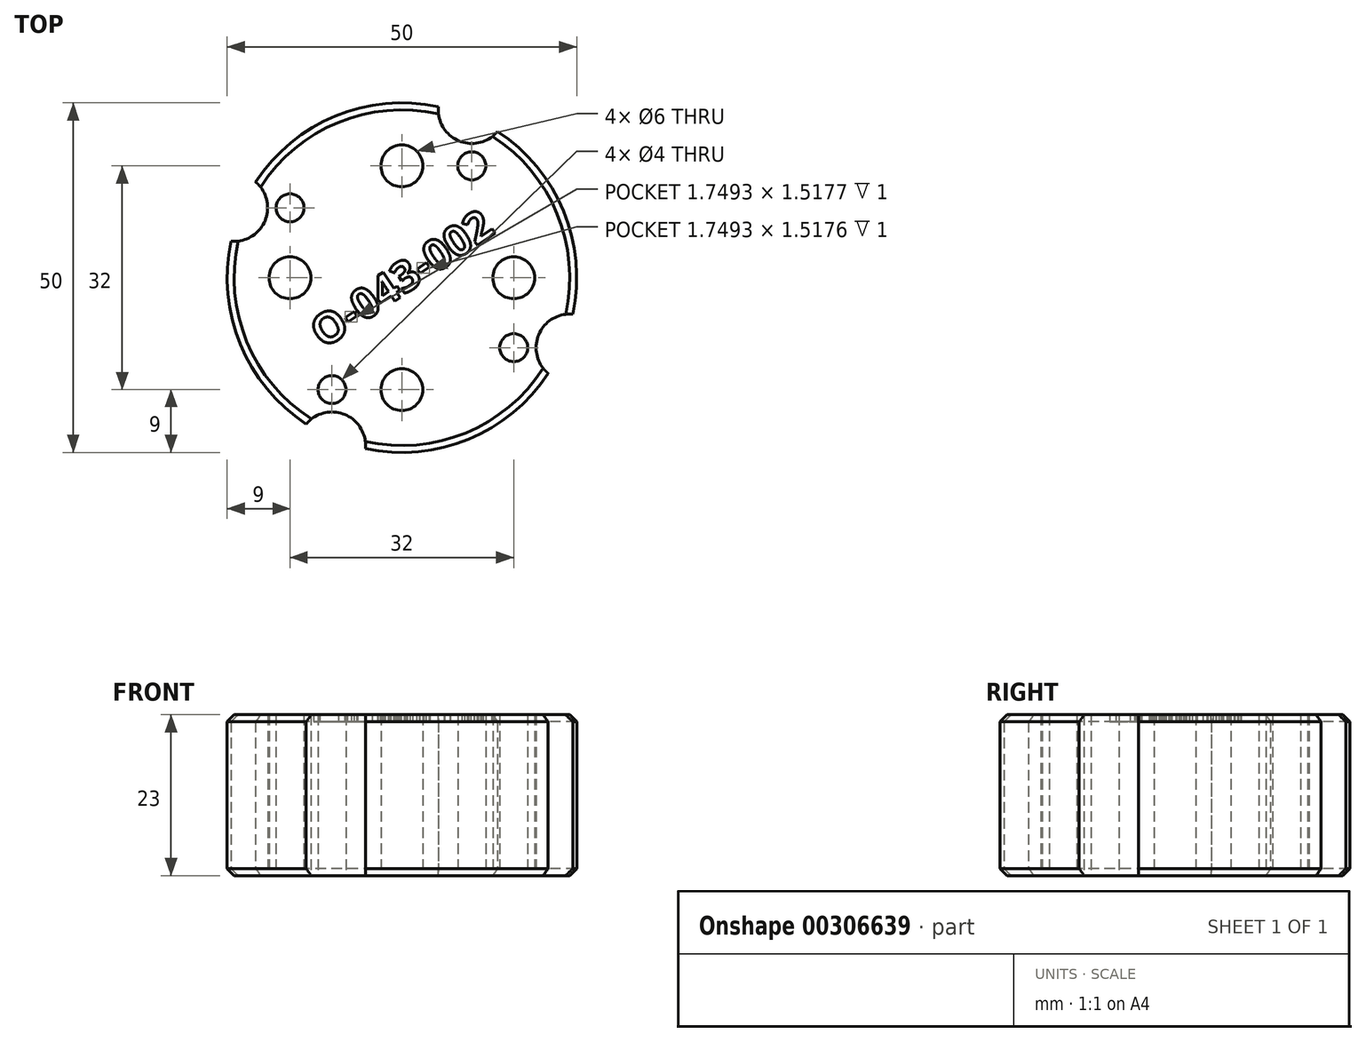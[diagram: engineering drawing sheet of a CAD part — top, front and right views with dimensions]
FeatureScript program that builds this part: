
annotation { "Feature Type Name" : "Feature", "Feature Type Description" : "" }
export const myFeature = defineFeature(function(context is Context, id is Id, definition is map)
    precondition{}
    {
        {
            var Q0;
            Q0=qCreatedBy(makeId("Top.planeOp"),FACE);
            var sketch = newSketch(context, id + "F0", { "sketchPlane" : qUnion([Q0])});
            skCircle(sketch, "E0", {"center": v(0, 16) * mm, "radius": 3 * mm});
            skPoint(sketch, "E1.center", {"position": v(0, 0) * mm});
            skCircle(sketch, "E2", {"center": v(10, 16) * mm, "radius": 2 * mm});
            skCircle(sketch, "E3.1.0", {"center": v(-16, 0) * mm, "radius": 3 * mm});
            skCircle(sketch, "E3.1.1", {"center": v(-16, 10) * mm, "radius": 2 * mm});
            skCircle(sketch, "E3.2.0", {"center": v(0, -16) * mm, "radius": 3 * mm});
            skCircle(sketch, "E3.2.1", {"center": v(-10, -16) * mm, "radius": 2 * mm});
            skCircle(sketch, "E3.3.0", {"center": v(16, 0) * mm, "radius": 3 * mm});
            skCircle(sketch, "E3.3.1", {"center": v(16, -10) * mm, "radius": 2 * mm});
            skCircle(sketch, "E4", {"center": v(0, 0) * mm, "radius": 25 * mm});
            skCircle(sketch, "E5", {"center": v(-24, 10) * mm, "radius": 4 * mm, "construction": true});
            skArc(sketch, "E6", {"start": v(-24.45, 5.22) * mm, "mid": v(-19.57, 8.15) * mm, "end": v(-20.92, 13.68) * mm});
            skCircle(sketch, "E7", {"center": v(-16, 10) * mm, "radius": 4.5 * mm, "construction": true});
            skArc(sketch, "E8.1.0", {"start": v(-5.22, -24.45) * mm, "mid": v(-8.15, -19.57) * mm, "end": v(-13.68, -20.92) * mm});
            skArc(sketch, "E8.2.0", {"start": v(24.45, -5.22) * mm, "mid": v(19.57, -8.15) * mm, "end": v(20.92, -13.68) * mm});
            skArc(sketch, "E8.3.0", {"start": v(5.22, 24.45) * mm, "mid": v(8.15, 19.57) * mm, "end": v(13.68, 20.92) * mm});
            skSolve(sketch);
        }
        {
            var Q0;
            Q0=makeQuery(id+"F0.imprint","IMPRINT",FACE,{"disambiguationData":[TD([[makeQuery(id+"F0.imprint","IMPRINT",EDGE,{"derivedFrom":sQuery(id+"F0.wireOp",EDGE,"E1.2.1")}),1.0]])]});
            var Q1;
            Q1=makeQuery(id+"F0.imprint","IMPRINT",FACE,{"disambiguationData":[TD([[makeQuery(id+"F0.imprint","IMPRINT",EDGE,{"derivedFrom":sQuery(id+"F0.wireOp",EDGE,"E1.3.1")}),1.0]])]});
            var Q2;
            Q2=makeQuery(id+"F0.imprint","IMPRINT",FACE,{"disambiguationData":[TD([[makeQuery(id+"F0.imprint","IMPRINT",EDGE,{"derivedFrom":sQuery(id+"F0.wireOp",EDGE,"E1.3.0")}),1.0]])]});
            var Q3;
            Q3=makeQuery(id+"F0.imprint","IMPRINT",FACE,{"disambiguationData":[TD([[makeQuery(id+"F0.imprint","IMPRINT",EDGE,{"derivedFrom":sQuery(id+"F0.wireOp",EDGE,"E1.2.0")}),1.0]])]});
            var Q4;
            Q4=makeQuery(id+"F0.imprint","IMPRINT",FACE,{"disambiguationData":[TD([[makeQuery(id+"F0.imprint","IMPRINT",EDGE,{"derivedFrom":sQuery(id+"F0.wireOp",EDGE,"5VkqoSrS-Cs9u-Mvgf-fKKW-AaG6FBBb1eUr")}),1.0]])]});
            var Q5;
            Q5=makeQuery(id+"F0.imprint","IMPRINT",FACE,{"disambiguationData":[TD([[makeQuery(id+"F0.imprint","IMPRINT",EDGE,{"derivedFrom":sQuery(id+"F0.wireOp",EDGE,"E1.1.0")}),1.0]])]});
            var Q6;
            Q6=makeQuery(id+"F0.imprint","IMPRINT",FACE,{"disambiguationData":[TD([[makeQuery(id+"F0.imprint","IMPRINT",EDGE,{"derivedFrom":sQuery(id+"F0.wireOp",EDGE,"E1.1.1")}),1.0]])]});
            var Q7;
            Q7=makeQuery(id+"F0.imprint","IMPRINT",FACE,{"disambiguationData":[TD([[makeQuery(id+"F0.imprint","IMPRINT",EDGE,{"derivedFrom":sQuery(id+"F0.wireOp",EDGE,"E0")}),-1.0]])]});
            extrude(context, id + "F1", {"entities" : qUnion([Q0, Q1, Q2, Q3, Q4, Q5, Q6, Q7]), "depth" : 23 * mm});
        }
        {
            var Q0;
            Q0=makeQuery(id+"F1.opExtrude","CAP_FACE",FACE,{"disambiguationData":[OSD([sQuery(id+"F0.wireOp",EDGE,"E0"),sQuery(id+"F0.wireOp",EDGE,"E2"),sQuery(id+"F0.wireOp",EDGE,"E3.1.0"),sQuery(id+"F0.wireOp",EDGE,"E3.1.1"),sQuery(id+"F0.wireOp",EDGE,"E3.2.0"),sQuery(id+"F0.wireOp",EDGE,"E3.2.1"),sQuery(id+"F0.wireOp",EDGE,"E3.3.0"),sQuery(id+"F0.wireOp",EDGE,"E3.3.1"),sQuery(id+"F0.wireOp",EDGE,"E4")])],"isStart":false});
            var sketch = newSketch(context, id + "F2", { "sketchPlane" : qUnion([Q0])});
            skText(sketch, "E9", { "text": "O-043-002", "fontName": "OpenSans-Bold.ttf"});
            skPoint(sketch, "E10", {"position": v(0, 0) * mm});
            const initialGuessF2  = {"E9": [-0.0112, -0.01022, 0.82904, 0.5592, 0.00441]};
            skSetInitialGuess(sketch, initialGuessF2);
            skSolve(sketch);
        }
        {
            var Q0;
            Q0 = qSketchRegion(id + "F2", true);
            extrude(context, id + "F3", {"entities" : qUnion([Q0]), "operationType" : NewBodyOperationType.REMOVE, "oppositeDirection" : true, "depth" : 1 * mm});
        }
        {
            var Q0;
            Q0=makeQuery(id+"F1.opExtrude","CAP_EDGE",EDGE,{"disambiguationData":[OSD([sQuery(id+"F0.wireOp",EDGE,"E4")])],"isStart":true});
            var Q1;
            Q1=makeQuery(id+"F1.opExtrude","CAP_EDGE",EDGE,{"disambiguationData":[OSD([sQuery(id+"F0.wireOp",EDGE,"E4")])],"isStart":false});
            chamfer(context, id + "F4", {"entities" : qUnion([Q0, Q1]), "width" : 1 * mm, "tangentPropagation" : true});
        }
    });
